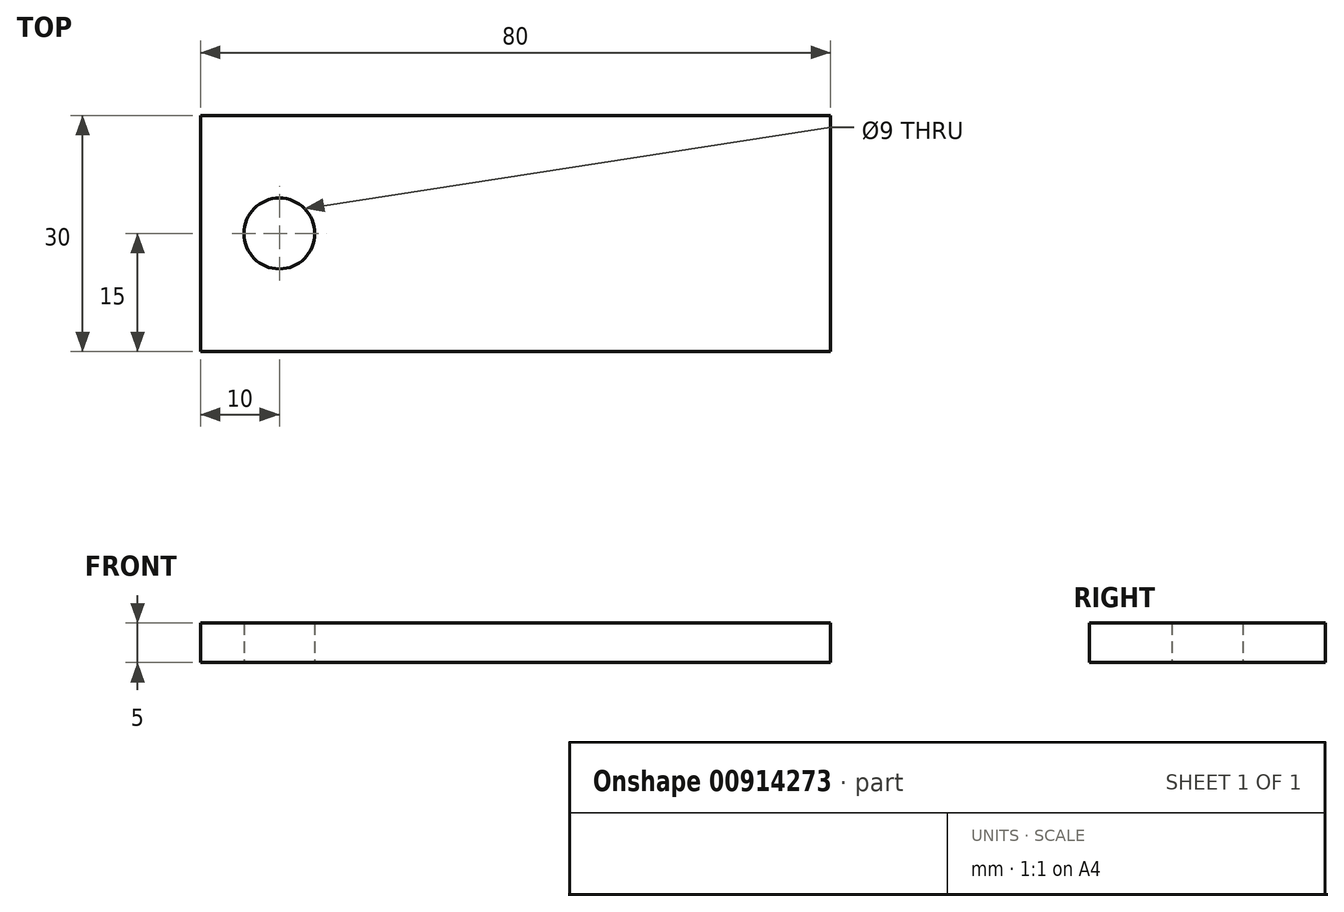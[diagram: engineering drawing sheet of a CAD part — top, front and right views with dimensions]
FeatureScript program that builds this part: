
annotation { "Feature Type Name" : "Feature", "Feature Type Description" : "" }
export const myFeature = defineFeature(function(context is Context, id is Id, definition is map)
    precondition{}
    {
        {
            var Q0;
            Q0=qCreatedBy(makeId("Top.planeOp"),FACE);
            var sketch = newSketch(context, id + "F0", { "sketchPlane" : qUnion([Q0])});
            skLineSegment(sketch, "E0.bottom", {"start": v(40, 15) * mm, "end": v(-40, 15) * mm});
            skLineSegment(sketch, "E0.top", {"start": v(40, -15) * mm, "end": v(-40, -15) * mm});
            skLineSegment(sketch, "E0.left", {"start": v(40, 15) * mm, "end": v(40, -15) * mm});
            skLineSegment(sketch, "E0.right", {"start": v(-40, 15) * mm, "end": v(-40, -15) * mm});
            skPoint(sketch, "E0.middle", {"position": v(0, 0) * mm});
            skCircle(sketch, "E1", {"center": v(-30, 0) * mm, "radius": 4.5 * mm});
            skSolve(sketch);
        }
        {
            var Q0;
            Q0=makeQuery(id+"F0.imprint","IMPRINT",FACE,{"disambiguationData":[TD([[makeQuery(id+"F0.imprint","IMPRINT",EDGE,{"derivedFrom":sQuery(id+"F0.wireOp",EDGE,"E0.bottom")}),1.0]])]});
            extrude(context, id + "F1", {"entities" : qUnion([Q0]), "depth" : 5 * mm, "offsetDistance" : 25 * mm});
        }
    });
